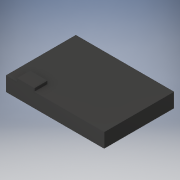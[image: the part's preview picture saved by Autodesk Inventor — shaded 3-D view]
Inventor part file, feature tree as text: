
AUTODESK INVENTOR PART (.ipt)
format: ipt  version: 2018 (Build 220112000, 112)  size: 103,424 bytes
history: native  units: in
note: dims shown in document units (in); Inventor stores cm internally (conversion verified against a paired STEP export)
features: extrude x2, sketch x2
ambient origin geometry x8: Origin, YZ Plane, XZ Plane, XY Plane, X Axis, Y Axis, Z Axis, Center Point
bodies: Solid1 (feature_tree)
feature tree (4):
  extrude  "Extrusion1"  Depth=1.2598in
  extrude  "Extrusion2"  Depth=0.315in
  sketch  "Sketch1"  dims[d0=1.7717in d1=1.2598in]
  sketch  "Sketch2"  dims[d2=0.2579in d3=0.0in d4=0.315in d5=0.2362in d6=0.1969in d7=0.0571in d8=0.0in]
